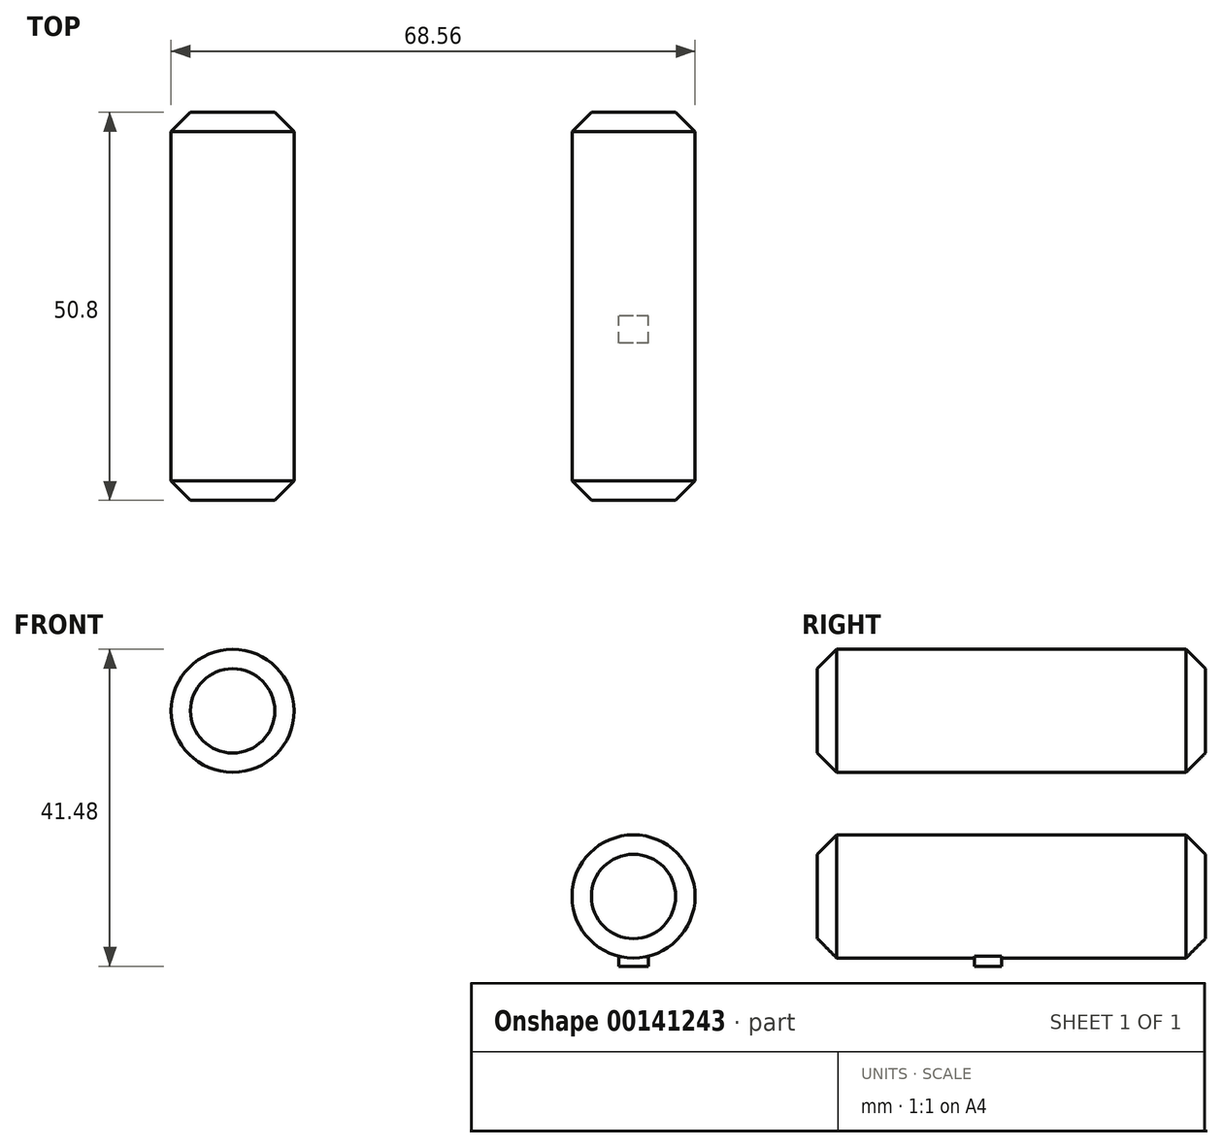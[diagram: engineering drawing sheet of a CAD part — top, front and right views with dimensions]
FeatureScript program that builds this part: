
annotation { "Feature Type Name" : "Feature", "Feature Type Description" : "" }
export const myFeature = defineFeature(function(context is Context, id is Id, definition is map)
    precondition{}
    {
        {
            var Q0;
            Q0=qCreatedBy(makeId("Front.planeOp"),FACE);
            var sketch = newSketch(context, id + "F0", { "sketchPlane" : qUnion([Q0])});
            skCircle(sketch, "E0", {"center": v(-52.46, 24.28) * mm, "radius": 8.05 * mm});
            skCircle(sketch, "E1", {"center": v(0, 0) * mm, "radius": 8.05 * mm});
            skSolve(sketch);
        }
        {
            var Q0;
            Q0 = qSketchRegion(id + "F0", true);
            extrude(context, id + "F1", {"entities" : qUnion([Q0]), "depth" : 50.8 * mm});
        }
        {
            var Q0;
            Q0=makeQuery(id+"F1.opExtrude","CAP_EDGE",EDGE,{"disambiguationData":[OSD([sQuery(id+"F0.wireOp",EDGE,"E0")])],"isStart":true});
            var Q1;
            Q1=makeQuery(id+"F1.opExtrude","CAP_FACE",FACE,{"disambiguationData":[OSD([sQuery(id+"F0.wireOp",EDGE,"E0")])],"isStart":false});
            chamfer(context, id + "F2", {"entities" : qUnion([Q0, Q1]), "width" : 2.54 * mm, "tangentPropagation" : true});
        }
        {
            var Q0;
            Q0=makeQuery(id+"F1.opExtrude","CAP_EDGE",EDGE,{"disambiguationData":[OSD([sQuery(id+"F0.wireOp",EDGE,"E1")])],"isStart":false});
            chamfer(context, id + "F3", {"entities" : qUnion([Q0]), "width" : 2.54 * mm, "tangentPropagation" : true});
        }
        {
            var Q0;
            Q0=makeQuery(id+"F1.opExtrude","CAP_EDGE",EDGE,{"disambiguationData":[OSD([sQuery(id+"F0.wireOp",EDGE,"E1")])],"isStart":true});
            chamfer(context, id + "F4", {"entities" : qUnion([Q0]), "width" : 2.54 * mm, "tangentPropagation" : true});
        }
        {
            var Q0;
            Q0=qCreatedBy(makeId("Top.planeOp"),FACE);
            var sketch = newSketch(context, id + "F5", { "sketchPlane" : qUnion([Q0])});
            skLineSegment(sketch, "E2.bottom", {"start": v(1.93, -26.67) * mm, "end": v(-1.93, -26.67) * mm});
            skLineSegment(sketch, "E2.top", {"start": v(1.93, -30.23) * mm, "end": v(-1.93, -30.23) * mm});
            skLineSegment(sketch, "E2.left", {"start": v(1.93, -26.67) * mm, "end": v(1.93, -30.23) * mm});
            skLineSegment(sketch, "E2.right", {"start": v(-1.93, -26.67) * mm, "end": v(-1.93, -30.23) * mm});
            skPoint(sketch, "E2.middle", {"position": v(0, -28.45) * mm});
            skSolve(sketch);
        }
        {
            var Q0;
            Q0 = qSketchRegion(id + "F5", true);
            extrude(context, id + "F6", {"entities" : qUnion([Q0]), "operationType" : NewBodyOperationType.ADD, "oppositeDirection" : true, "depth" : 9.14 * mm});
        }
        {
            var Q0;
            Q0=makeQuery(id+"F1.opExtrude","SWEPT_BODY",BODY,{"disambiguationData":[OSD([sQuery(id+"F0.wireOp",EDGE,"E1")])]});
            transform(context, id + "F7", {"entities" : qUnion([Q0]), "transformType" : TransformType.TRANSLATION_3D, "dx" : 0 * mm, "dy" : 0 * mm, "dz" : 0 * mm, "makeCopy" : true});
        }
    });
